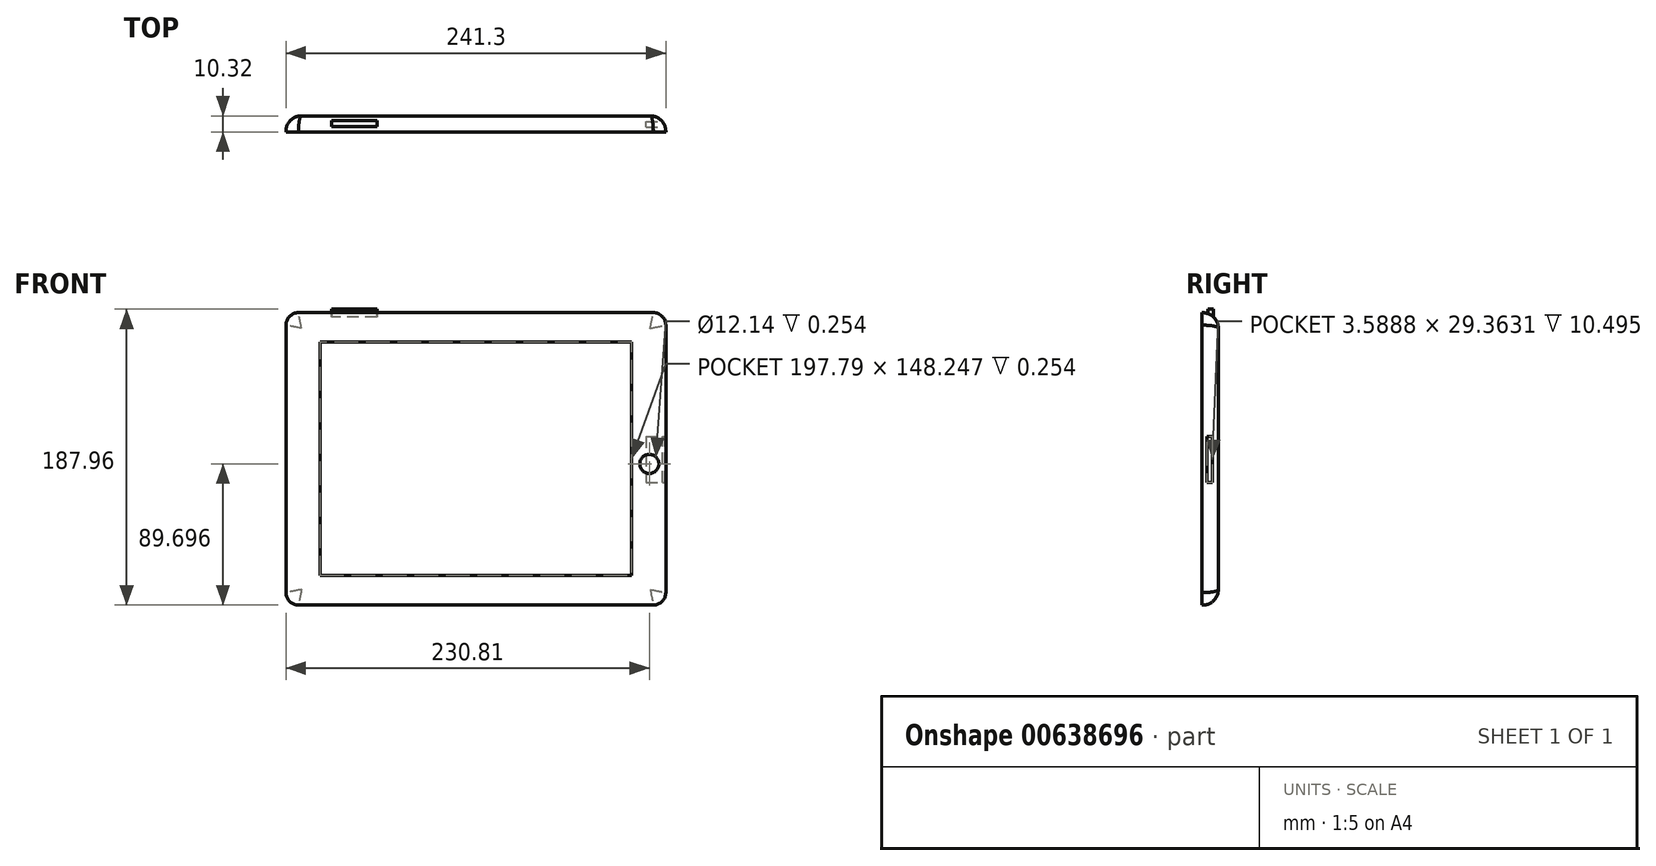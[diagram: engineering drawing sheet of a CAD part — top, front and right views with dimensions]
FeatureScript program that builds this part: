
annotation { "Feature Type Name" : "Feature", "Feature Type Description" : "" }
export const myFeature = defineFeature(function(context is Context, id is Id, definition is map)
    precondition{}
    {
        {
            var Q0;
            Q0=qCreatedBy(makeId("Front.planeOp"),FACE);
            var sketch = newSketch(context, id + "F0", { "sketchPlane" : qUnion([Q0])});
            skLineSegment(sketch, "E0.bottom", {"start": v(7.94, 0) * mm, "end": v(233.36, 0) * mm});
            skLineSegment(sketch, "E0.top", {"start": v(7.94, 185.74) * mm, "end": v(233.36, 185.74) * mm});
            skLineSegment(sketch, "E0.left", {"start": v(0, 7.94) * mm, "end": v(0, 177.8) * mm});
            skLineSegment(sketch, "E0.right", {"start": v(241.3, 7.94) * mm, "end": v(241.3, 177.8) * mm});
            skPoint(sketch, "E1.visualSharp", {"position": v(0, 185.74) * mm});
            skArc(sketch, "E1.filletArc", {"start": v(7.94, 185.74) * mm, "mid": v(2.32, 183.41) * mm, "end": v(0, 177.8) * mm});
            skPoint(sketch, "E2.visualSharp", {"position": v(0, 0) * mm});
            skArc(sketch, "E2.filletArc", {"start": v(0, 7.94) * mm, "mid": v(2.32, 2.32) * mm, "end": v(7.94, 0) * mm});
            skPoint(sketch, "E3.visualSharp", {"position": v(241.3, 185.74) * mm});
            skArc(sketch, "E3.filletArc", {"start": v(241.3, 177.8) * mm, "mid": v(238.98, 183.41) * mm, "end": v(233.36, 185.74) * mm});
            skPoint(sketch, "E4.visualSharp", {"position": v(241.3, 0) * mm});
            skArc(sketch, "E4.filletArc", {"start": v(233.36, 0) * mm, "mid": v(238.98, 2.32) * mm, "end": v(241.3, 7.94) * mm});
            skSolve(sketch);
        }
        {
            var Q0;
            Q0 = qSketchRegion(id + "F0", true);
            extrude(context, id + "F1", {"entities" : qUnion([Q0]), "depth" : 10.32 * mm, "offsetDistance" : 25.4 * mm});
        }
        {
            var Q0;
            Q0=makeQuery(id+"F1.opExtrude","CAP_EDGE",EDGE,{"disambiguationData":[OSD([sQuery(id+"F0.wireOp",EDGE,"E0.top")])],"isStart":true});
            fillet(context, id + "F2", {"entities" : qUnion([Q0]), "radius" : 9.9 * mm, "tangentPropagation" : true, "allowEdgeOverflow" : false});
        }
        {
            var Q0;
            Q0=qCreatedBy(makeId("Right.planeOp"),FACE);
            cPlane(context, id + "F3", {"entities" : qUnion([Q0]), "cplaneType" : CPlaneType.OFFSET, "offset" : 254 * mm, "width" : 152.4 * mm, "height" : 152.4 * mm});
        }
        {
            var Q0;
            Q0=qCreatedBy(id+"F3.planeOp",FACE);
            var sketch = newSketch(context, id + "F4", { "sketchPlane" : qUnion([Q0])});
            skLineSegment(sketch, "E5.bottom", {"start": v(-7.26, 107.17) * mm, "end": v(-3.68, 107.17) * mm});
            skLineSegment(sketch, "E5.top", {"start": v(-7.26, 77.81) * mm, "end": v(-3.68, 77.81) * mm});
            skLineSegment(sketch, "E5.left", {"start": v(-7.26, 107.17) * mm, "end": v(-7.26, 77.81) * mm});
            skLineSegment(sketch, "E5.right", {"start": v(-3.68, 107.17) * mm, "end": v(-3.68, 77.81) * mm});
            skPoint(sketch, "E5.middle", {"position": v(-5.47, 92.5) * mm});
            skSolve(sketch);
        }
        {
            var Q0;
            Q0 = qSketchRegion(id + "F4", true);
            extrude(context, id + "F5", {"entities" : qUnion([Q0]), "operationType" : NewBodyOperationType.REMOVE, "oppositeDirection" : true, "depth" : 25.4 * mm, "offsetDistance" : 25.4 * mm});
        }
        {
            var Q0;
            Q0=qCreatedBy(makeId("Top.planeOp"),FACE);
            cPlane(context, id + "F6", {"entities" : qUnion([Q0]), "cplaneType" : CPlaneType.OFFSET, "offset" : 203.2 * mm, "width" : 152.4 * mm, "height" : 152.4 * mm});
        }
        {
            var Q0;
            Q0=qCreatedBy(id+"F6.planeOp",FACE);
            var sketch = newSketch(context, id + "F7", { "sketchPlane" : qUnion([Q0])});
            skLineSegment(sketch, "E6.bottom", {"start": v(28.88, -3.14) * mm, "end": v(57.81, -3.14) * mm});
            skLineSegment(sketch, "E6.top", {"start": v(28.88, -6.67) * mm, "end": v(57.81, -6.67) * mm});
            skLineSegment(sketch, "E6.left", {"start": v(28.88, -3.14) * mm, "end": v(28.88, -6.67) * mm});
            skLineSegment(sketch, "E6.right", {"start": v(57.81, -3.14) * mm, "end": v(57.81, -6.67) * mm});
            skEllipticalArc(sketch, "E7.0", {"construction": true});
            skLineSegment(sketch, "E8.0", {"start": v(0, -10.32) * mm, "end": v(0, -9.9) * mm, "construction": true});
            const initialGuessF7  = {"E7.0": [0.009906, -0.009906, 0, 1, 0.009906, 0.0019685000000000154, 0, 1.5707963267948966]};
            skSetInitialGuess(sketch, initialGuessF7);
            skSolve(sketch);
        }
        {
            var Q0;
            Q0 = qSketchRegion(id + "F7", true);
            extrude(context, id + "F8", {"entities" : qUnion([Q0]), "operationType" : NewBodyOperationType.ADD, "oppositeDirection" : true, "depth" : 25.4 * mm, "offsetDistance" : 25.4 * mm});
        }
        {
            var Q0;
            Q0 = qSketchRegion(id + "F7", true);
            extrude(context, id + "F9", {"entities" : qUnion([Q0]), "operationType" : NewBodyOperationType.REMOVE, "oppositeDirection" : true, "depth" : 15.24 * mm, "offsetDistance" : 25.4 * mm});
        }
        {
            var Q0;
            Q0=makeQuery(id+"F1.opExtrude","CAP_FACE",FACE,{"disambiguationData":[OSD([sQuery(id+"F0.wireOp",EDGE,"E0.bottom"),sQuery(id+"F0.wireOp",EDGE,"E0.top"),sQuery(id+"F0.wireOp",EDGE,"E0.left"),sQuery(id+"F0.wireOp",EDGE,"E0.right"),sQuery(id+"F0.wireOp",EDGE,"E1.filletArc"),sQuery(id+"F0.wireOp",EDGE,"E2.filletArc"),sQuery(id+"F0.wireOp",EDGE,"E3.filletArc"),sQuery(id+"F0.wireOp",EDGE,"E4.filletArc")])],"isStart":false});
            var sketch = newSketch(context, id + "F10", { "sketchPlane" : qUnion([Q0])});
            skLineSegment(sketch, "E9.bottom", {"start": v(21.77, 167) * mm, "end": v(219.56, 167) * mm});
            skLineSegment(sketch, "E9.top", {"start": v(21.77, 18.75) * mm, "end": v(219.56, 18.75) * mm});
            skLineSegment(sketch, "E9.left", {"start": v(21.77, 167) * mm, "end": v(21.77, 18.75) * mm});
            skLineSegment(sketch, "E9.right", {"start": v(219.56, 167) * mm, "end": v(219.56, 18.75) * mm});
            skLineSegment(sketch, "E10.0", {"start": v(0, 7.94) * mm, "end": v(0, 177.8) * mm, "construction": true});
            skLineSegment(sketch, "E11.0", {"start": v(7.94, 185.74) * mm, "end": v(233.36, 185.74) * mm, "construction": true});
            skLineSegment(sketch, "E12.0", {"start": v(241.3, 7.94) * mm, "end": v(241.3, 177.8) * mm, "construction": true});
            skLineSegment(sketch, "E13.0", {"start": v(7.94, 0) * mm, "end": v(233.36, 0) * mm, "construction": true});
            skCircle(sketch, "E14", {"center": v(230.8, 89.7) * mm, "radius": 6.07 * mm});
            skSolve(sketch);
        }
        {
            var Q0;
            Q0 = qSketchRegion(id + "F10", true);
            var Q1;
            Q1 = qConstructionFilter(qBodyType(qCreatedBy(id + "F10" ,EDGE), BodyType.WIRE), ConstructionObject.NO);
            extrude(context, id + "F11", {"entities" : qUnion([Q0]), "operationType" : NewBodyOperationType.REMOVE, "surfaceEntities" : qUnion([Q1]), "oppositeDirection" : true, "depth" : 0.25 * mm, "offsetDistance" : 25.4 * mm});
        }
    });
